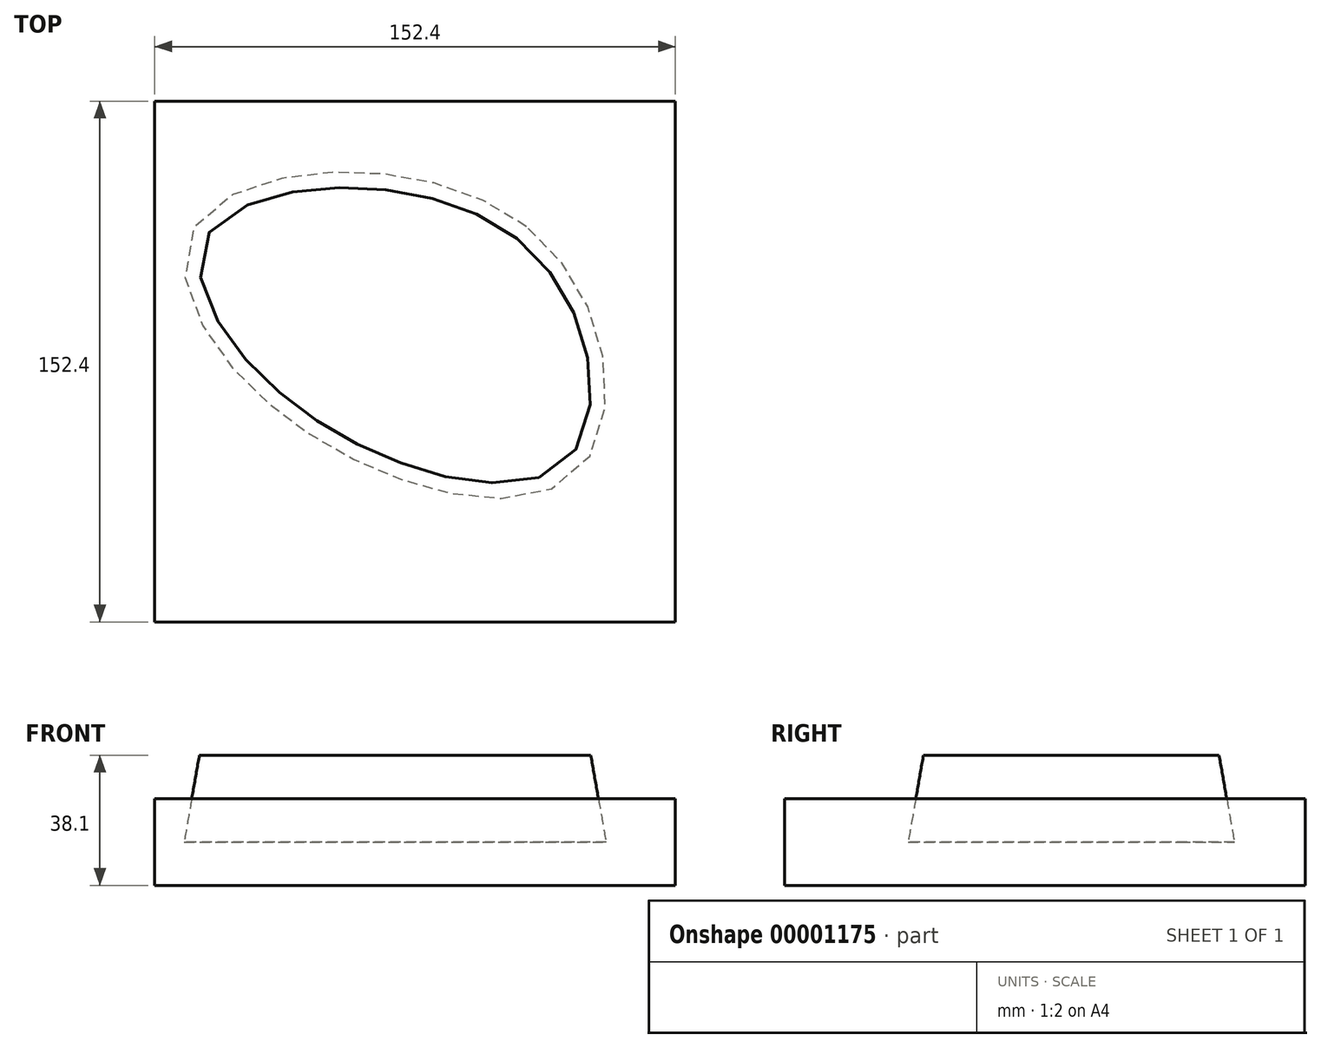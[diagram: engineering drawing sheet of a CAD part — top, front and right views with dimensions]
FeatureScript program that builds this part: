
annotation { "Feature Type Name" : "Feature", "Feature Type Description" : "" }
export const myFeature = defineFeature(function(context is Context, id is Id, definition is map)
    precondition{}
    {
        {
            var Q0;
            Q0=qCreatedBy(makeId("Top.planeOp"),FACE);
            var sketch = newSketch(context, id + "F0", { "sketchPlane" : qUnion([Q0])});
            skLineSegment(sketch, "E0.rect.bottom", {"start": v(-76.2, -76.2) * mm, "end": v(76.2, -76.2) * mm});
            skLineSegment(sketch, "E0.rect.top", {"start": v(-76.2, 76.2) * mm, "end": v(76.2, 76.2) * mm});
            skLineSegment(sketch, "E0.rect.left", {"start": v(-76.2, -76.2) * mm, "end": v(-76.2, 76.2) * mm});
            skLineSegment(sketch, "E0.rect.right", {"start": v(76.2, -76.2) * mm, "end": v(76.2, 76.2) * mm});
            skPoint(sketch, "E0.rect.middle", {"position": v(0, 0) * mm});
            skSolve(sketch);
        }
        {
            var Q0;
            Q0 = qSketchRegion(id + "F0", true);
            extrude(context, id + "F1", {"entities" : qUnion([Q0]), "endBound" : BoundingType.SYMMETRIC, "depth" : 25.4 * mm});
        }
        {
            var Q0;
            Q0=qCreatedBy(makeId("Top.planeOp"),FACE);
            var sketch = newSketch(context, id + "F2", { "sketchPlane" : qUnion([Q0])});
            skFitSpline(sketch, "E1", {"points": [v(-38.38, -15.93) * mm, v(-63.24, 41.3) * mm, v(32.58, 39.5) * mm, v(47.34, -32.5) * mm, v(-38.38, -15.93) * mm]});
            skSolve(sketch);
        }
        {
            var Q0;
            Q0=makeQuery(id+"F2.imprint","IMPRINT",FACE,{"disambiguationData":[TD([[makeQuery(id+"F2.imprint","IMPRINT",EDGE,{"derivedFrom":sQuery(id+"F2.wireOp",EDGE,"E1")}),-1.0]])]});
            extrude(context, id + "F3", {"entities" : qUnion([Q0]), "depth" : 25.4 * mm, "hasDraft" : true, "draftAngle" : 10 * degree, "draftPullDirection" : true});
        }
    });
